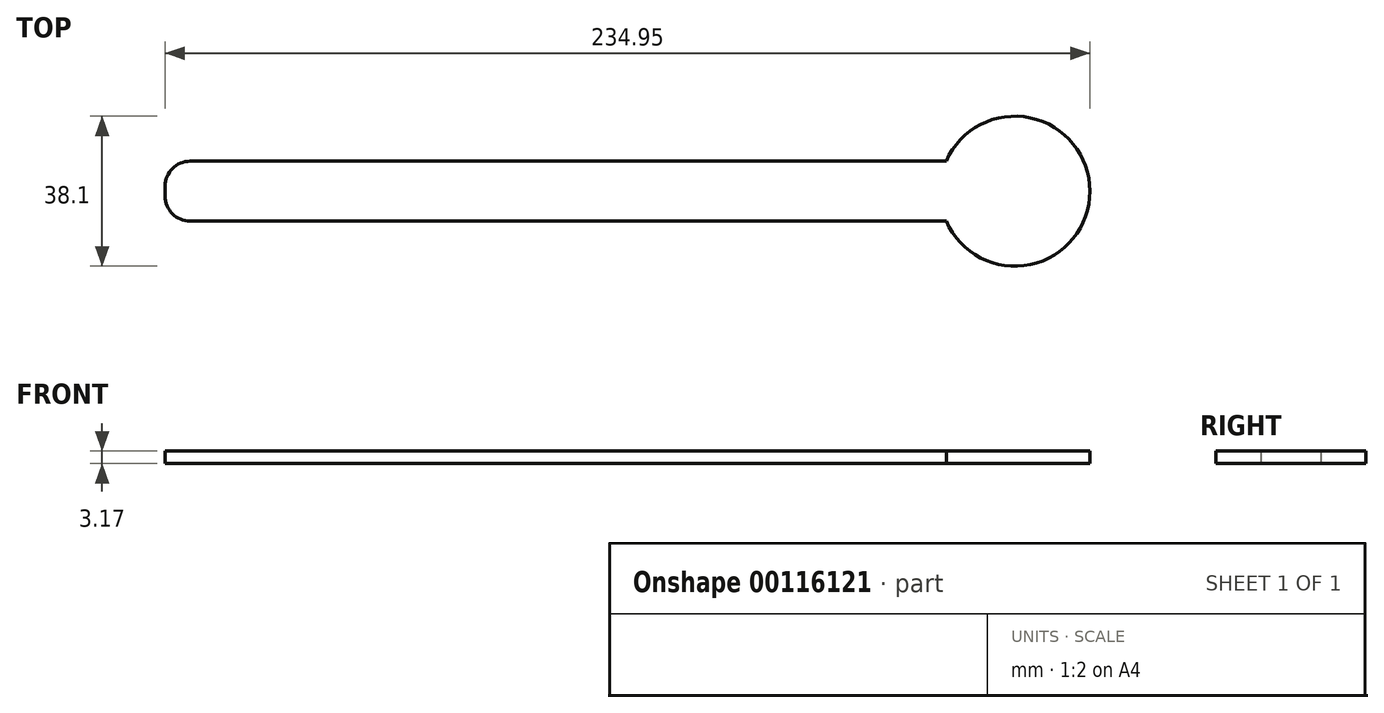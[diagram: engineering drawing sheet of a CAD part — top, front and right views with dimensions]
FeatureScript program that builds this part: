
annotation { "Feature Type Name" : "Feature", "Feature Type Description" : "" }
export const myFeature = defineFeature(function(context is Context, id is Id, definition is map)
    precondition{}
    {
        {
            var Q0;
            Q0=qCreatedBy(makeId("Top.planeOp"),FACE);
            var sketch = newSketch(context, id + "F0", { "sketchPlane" : qUnion([Q0])});
            skLineSegment(sketch, "E0.bottom", {"start": v(6.35, 0) * mm, "end": v(198.44, 0) * mm});
            skLineSegment(sketch, "E0.top", {"start": v(6.35, 15.24) * mm, "end": v(198.44, 15.24) * mm});
            skLineSegment(sketch, "E0.left", {"start": v(0, 6.35) * mm, "end": v(0, 8.9) * mm});
            skPoint(sketch, "E1", {"position": v(12.7, 7.62) * mm});
            skPoint(sketch, "E2", {"position": v(215.9, 7.62) * mm});
            skArc(sketch, "E3", {"start": v(198.44, 0) * mm, "mid": v(234.95, 7.62) * mm, "end": v(198.44, 15.24) * mm});
            skPoint(sketch, "E4.visualSharp", {"position": v(0, 15.24) * mm});
            skArc(sketch, "E4.filletArc", {"start": v(6.35, 15.24) * mm, "mid": v(1.86, 13.38) * mm, "end": v(0, 8.9) * mm});
            skPoint(sketch, "E5.visualSharp", {"position": v(0, 0) * mm});
            skArc(sketch, "E5.filletArc", {"start": v(0, 6.35) * mm, "mid": v(1.86, 1.86) * mm, "end": v(6.35, 0) * mm});
            skSolve(sketch);
        }
        {
            var Q0;
            Q0=makeQuery(id+"F0.imprint","IMPRINT",FACE,{"disambiguationData":[TD([[makeQuery(id+"F0.imprint","IMPRINT",EDGE,{"derivedFrom":sQuery(id+"F0.wireOp",EDGE,"E0.left")}),-1.0]])]});
            extrude(context, id + "F1", {"entities" : qUnion([Q0]), "depth" : 3.17 * mm});
        }
    });
